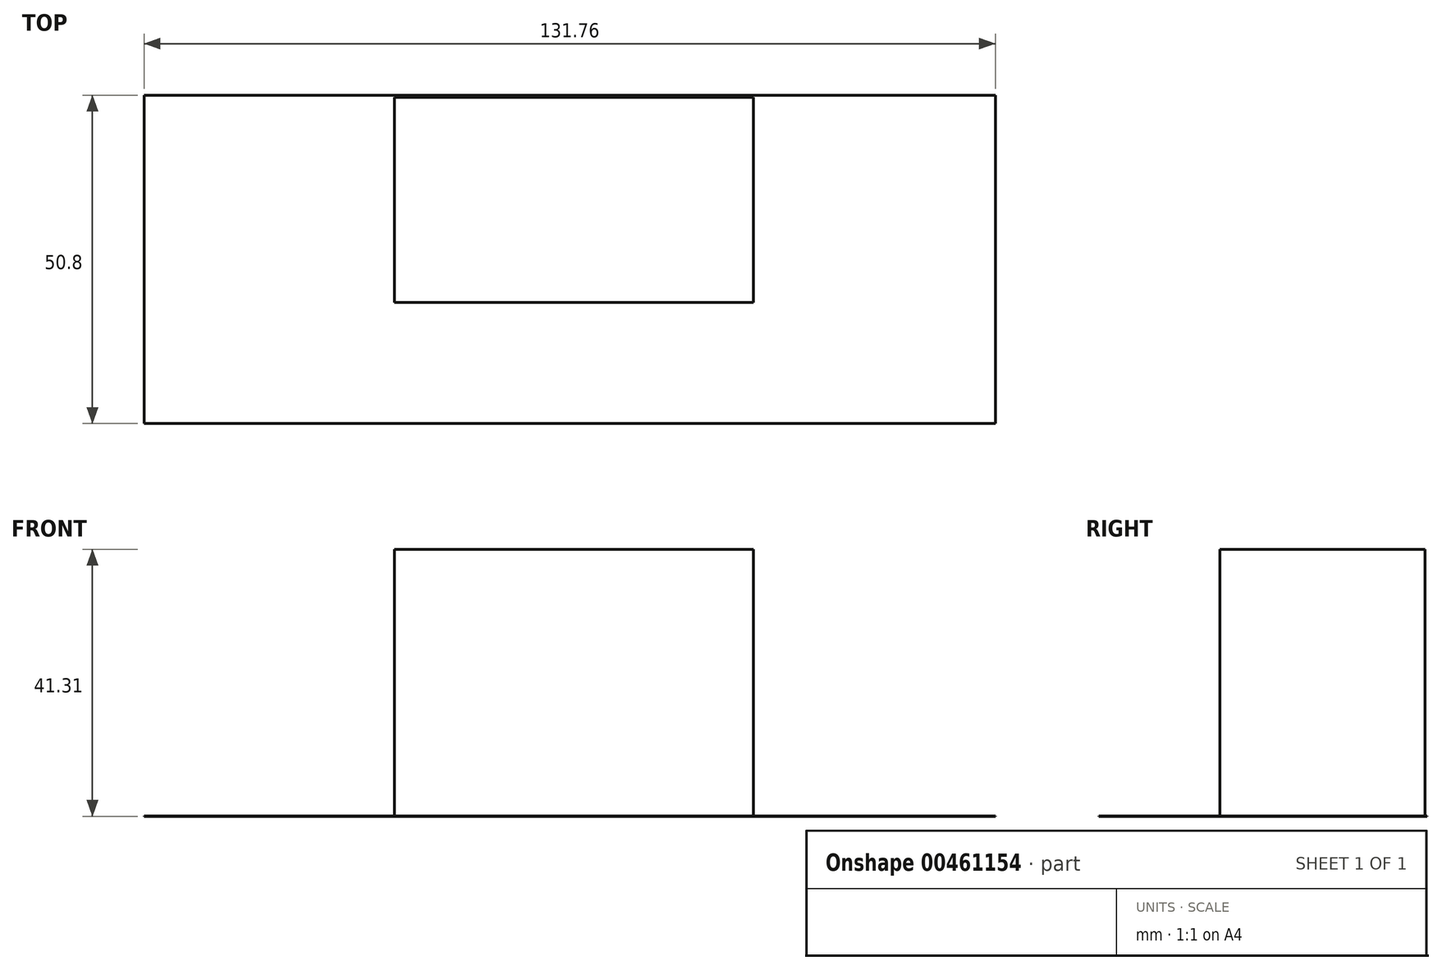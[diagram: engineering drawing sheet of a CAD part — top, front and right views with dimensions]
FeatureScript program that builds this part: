
annotation { "Feature Type Name" : "Feature", "Feature Type Description" : "" }
export const myFeature = defineFeature(function(context is Context, id is Id, definition is map)
    precondition{}
    {
        {
            var Q0;
            Q0=qCreatedBy(makeId("Top.planeOp"),FACE);
            var sketch = newSketch(context, id + "F0", { "sketchPlane" : qUnion([Q0])});
            skLineSegment(sketch, "E0.bottom", {"start": v(-102.27, 17.71) * mm, "end": v(29.5, 17.71) * mm});
            skLineSegment(sketch, "E0.top", {"start": v(-102.27, -33.09) * mm, "end": v(29.5, -33.09) * mm});
            skLineSegment(sketch, "E0.left", {"start": v(-102.27, 17.71) * mm, "end": v(-102.27, -33.09) * mm});
            skLineSegment(sketch, "E0.right", {"start": v(29.5, 17.71) * mm, "end": v(29.5, -33.09) * mm});
            skSolve(sketch);
        }
        {
            var Q0;
            Q0=makeQuery(id+"F0.imprint","IMPRINT",FACE,{"disambiguationData":[TD([[makeQuery(id+"F0.imprint","IMPRINT",EDGE,{"derivedFrom":sQuery(id+"F0.wireOp",EDGE,"E0.bottom")}),-1.0]])]});
            extrude(context, id + "F1", {"entities" : qUnion([Q0]), "depth" : 7 / 203.2 * mm});
        }
        {
            var Q0;
            Q0=makeQuery(id+"F1.opExtrude","CAP_FACE",FACE,{"disambiguationData":[OSD([sQuery(id+"F0.wireOp",EDGE,"E0.bottom"),sQuery(id+"F0.wireOp",EDGE,"E0.top"),sQuery(id+"F0.wireOp",EDGE,"E0.left"),sQuery(id+"F0.wireOp",EDGE,"E0.right")])],"isStart":false});
            var sketch = newSketch(context, id + "F2", { "sketchPlane" : qUnion([Q0])});
            skLineSegment(sketch, "E1", {"start": v(29.5, 17.71) * mm, "end": v(-8.6, 17.71) * mm});
            skSolve(sketch);
        }
        {
            var Q0;
            {var subQ2=sQuery(id+"F2.wireOp",EDGE,"E1");Q0=makeQuery(id+"F2.imprint","IMPRINT",FACE,{"disambiguationData":[TD([[makeQuery(id+"F2.imprint","IMPRINT",EDGE,{"derivedFrom":subQ2}),-1.0]])]});}
            var sketch = newSketch(context, id + "F3", { "sketchPlane" : qUnion([Q0])});
            skLineSegment(sketch, "E2.bottom", {"start": v(-7.96, 17.39) * mm, "end": v(-63.53, 17.39) * mm});
            skLineSegment(sketch, "E2.top", {"start": v(-7.96, -14.36) * mm, "end": v(-63.53, -14.36) * mm});
            skLineSegment(sketch, "E2.left", {"start": v(-7.96, 17.39) * mm, "end": v(-7.96, -14.36) * mm});
            skLineSegment(sketch, "E2.right", {"start": v(-63.53, 17.39) * mm, "end": v(-63.53, -14.36) * mm});
            skSolve(sketch);
        }
        {
            var Q0;
            Q0=qSketchRegion(id+"F3",true);
            extrude(context, id + "F4", {"entities" : qUnion([Q0]), "operationType" : NewBodyOperationType.ADD, "depth" : 41.27 * mm});
        }
    });
